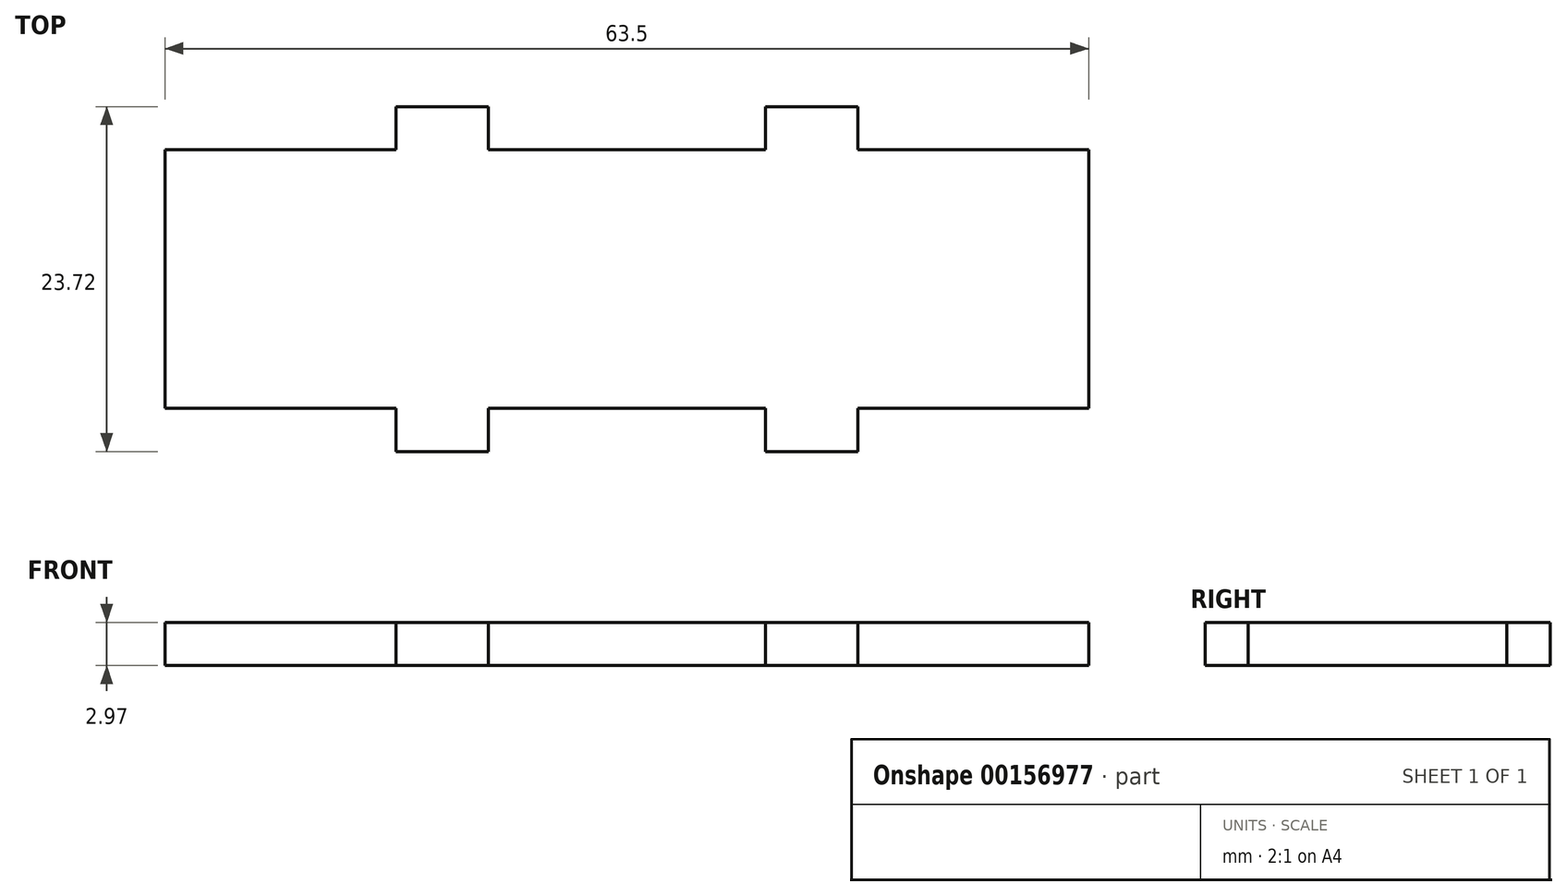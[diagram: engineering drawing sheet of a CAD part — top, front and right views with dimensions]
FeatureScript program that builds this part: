
annotation { "Feature Type Name" : "Feature", "Feature Type Description" : "" }
export const myFeature = defineFeature(function(context is Context, id is Id, definition is map)
    precondition{}
    {
        {
            var Q0;
            Q0=qCreatedBy(makeId("Top.planeOp"),FACE);
            var sketch = newSketch(context, id + "F0", { "sketchPlane" : qUnion([Q0])});
            skLineSegment(sketch, "E0.bottom", {"start": v(31.75, 8.9) * mm, "end": v(-31.75, 8.9) * mm});
            skLineSegment(sketch, "E0.top", {"start": v(31.75, -8.9) * mm, "end": v(-31.75, -8.9) * mm});
            skLineSegment(sketch, "E0.left", {"start": v(31.75, 8.9) * mm, "end": v(31.75, -8.9) * mm});
            skLineSegment(sketch, "E0.right", {"start": v(-31.75, 8.9) * mm, "end": v(-31.75, -8.9) * mm});
            skPoint(sketch, "E0.middle", {"position": v(0, 0) * mm});
            skLineSegment(sketch, "E1", {"start": v(0, 0) * mm, "end": v(-31.75, 0) * mm, "construction": true});
            skLineSegment(sketch, "E2", {"start": v(0, 0) * mm, "end": v(31.75, 0) * mm, "construction": true});
            skLineSegment(sketch, "E3", {"start": v(0, 0) * mm, "end": v(0, -8.9) * mm, "construction": true});
            skLineSegment(sketch, "E4", {"start": v(0, 0) * mm, "end": v(0, 8.9) * mm, "construction": true});
            skLineSegment(sketch, "E5.bottom", {"start": v(-9.53, 11.86) * mm, "end": v(-15.88, 11.86) * mm});
            skLineSegment(sketch, "E5.top", {"start": v(-9.52, 5.92) * mm, "end": v(-15.88, 5.92) * mm});
            skLineSegment(sketch, "E5.left", {"start": v(-9.53, 11.86) * mm, "end": v(-9.52, 5.92) * mm});
            skLineSegment(sketch, "E5.right", {"start": v(-15.88, 11.86) * mm, "end": v(-15.88, 5.92) * mm});
            skPoint(sketch, "E5.middle", {"position": v(-12.7, 8.9) * mm});
            skLineSegment(sketch, "E6.MirrorCS", {"start": v(9.53, 11.86) * mm, "end": v(9.52, 5.92) * mm});
            skLineSegment(sketch, "E7.MirrorCS", {"start": v(15.88, 11.86) * mm, "end": v(15.88, 5.92) * mm});
            skLineSegment(sketch, "E8.MirrorCS", {"start": v(9.53, 11.86) * mm, "end": v(15.88, 11.86) * mm});
            skLineSegment(sketch, "E9.MirrorCS", {"start": v(-9.53, -11.86) * mm, "end": v(-15.88, -11.86) * mm});
            skLineSegment(sketch, "E10.MirrorCS", {"start": v(-15.88, -11.86) * mm, "end": v(-15.88, -5.92) * mm});
            skLineSegment(sketch, "E11.MirrorCS", {"start": v(-9.53, -11.86) * mm, "end": v(-9.52, -5.92) * mm});
            skLineSegment(sketch, "E12.MirrorCS", {"start": v(9.53, -11.86) * mm, "end": v(9.52, -5.92) * mm});
            skLineSegment(sketch, "E13.MirrorCS", {"start": v(9.53, -11.86) * mm, "end": v(15.88, -11.86) * mm});
            skLineSegment(sketch, "E14.MirrorCS", {"start": v(15.88, -11.86) * mm, "end": v(15.88, -5.92) * mm});
            skSolve(sketch);
        }
        {
            var Q0;
            Q0 = qSketchRegion(id + "F0", true);
            extrude(context, id + "F1", {"entities" : qUnion([Q0]), "depth" : 2.97 * mm});
        }
    });
